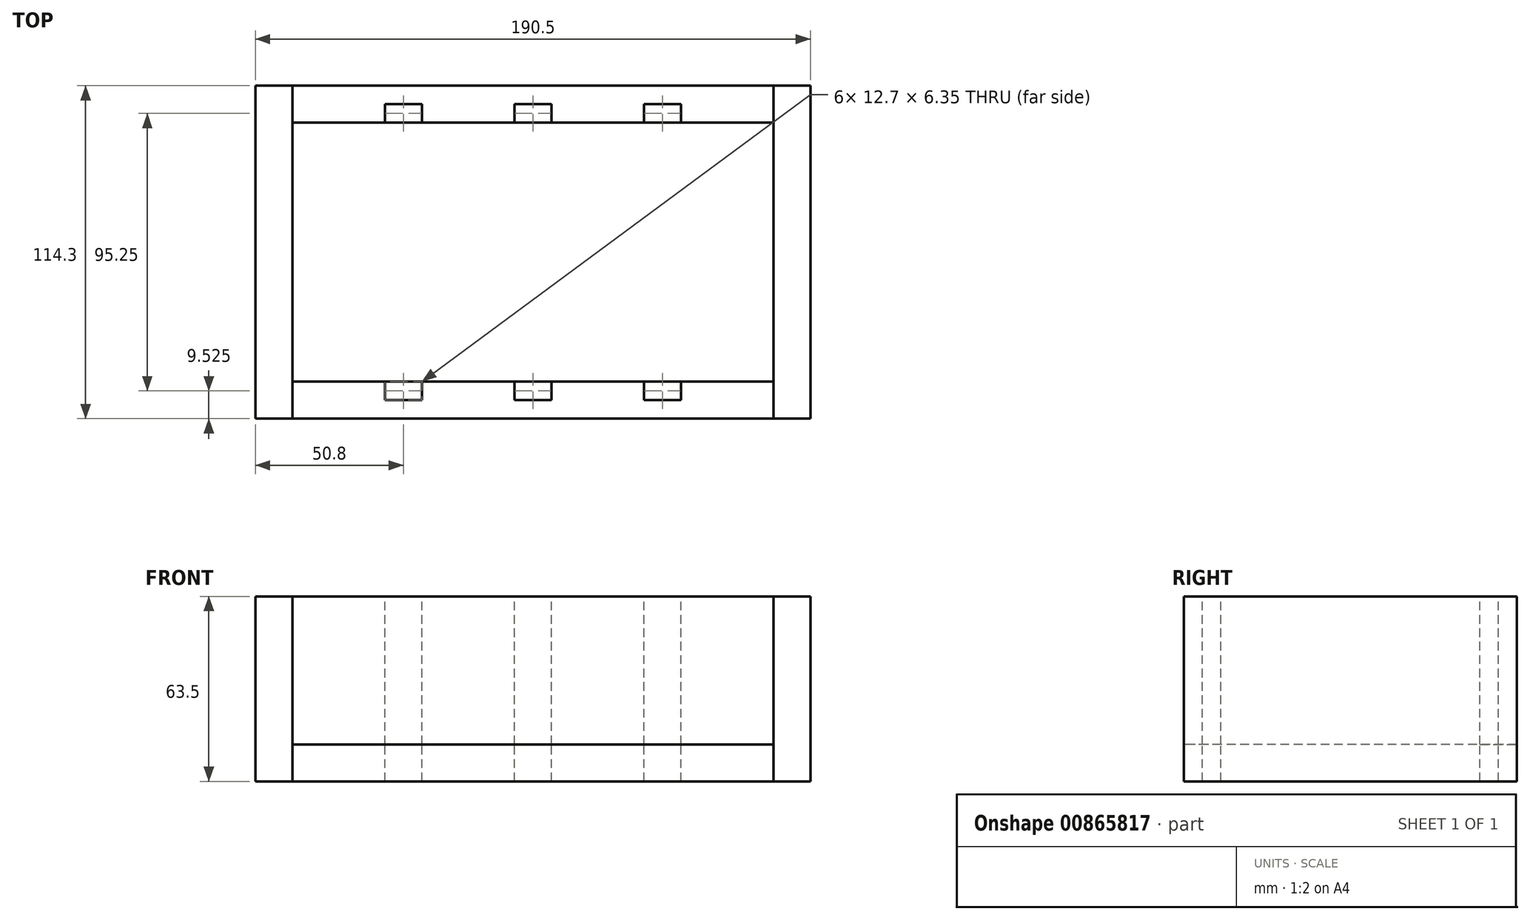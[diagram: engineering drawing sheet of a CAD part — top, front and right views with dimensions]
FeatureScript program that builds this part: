
annotation { "Feature Type Name" : "Feature", "Feature Type Description" : "" }
export const myFeature = defineFeature(function(context is Context, id is Id, definition is map)
    precondition{}
    {
        {
            var Q0;
            Q0=qCreatedBy(makeId("Top.planeOp"),FACE);
            var sketch = newSketch(context, id + "F0", { "sketchPlane" : qUnion([Q0])});
            skLineSegment(sketch, "E0.bottom", {"start": v(-82.55, 57.15) * mm, "end": v(82.55, 57.15) * mm});
            skLineSegment(sketch, "E0.top", {"start": v(-82.55, -57.15) * mm, "end": v(82.55, -57.15) * mm});
            skLineSegment(sketch, "E0.left", {"start": v(-82.55, 57.15) * mm, "end": v(-82.55, -57.15) * mm});
            skLineSegment(sketch, "E0.right", {"start": v(82.55, 57.15) * mm, "end": v(82.55, -57.15) * mm});
            skPoint(sketch, "E0.middle", {"position": v(0, 0) * mm});
            skSolve(sketch);
        }
        {
            var Q0;
            Q0=qCreatedBy(makeId("Front.planeOp"),FACE);
            var Q1;
            Q1=sQuery(id+"F0.wireOp",EDGE,"E0.bottom");
            cPlane(context, id + "F1", {"entities" : qUnion([Q0, Q1]), "cplaneType" : CPlaneType.LINE_ANGLE, "offset" : 25.4 * mm, "angle" : 0 * degree, "oppositeDirection" : true, "width" : 152.4 * mm, "height" : 152.4 * mm});
        }
        {
            var Q0;
            Q0=qCreatedBy(id+"F1.planeOp",FACE);
            var sketch = newSketch(context, id + "F2", { "sketchPlane" : qUnion([Q0])});
            skLineSegment(sketch, "E1.0.1", {"start": v(82.55, 0) * mm, "end": v(-82.55, 0) * mm});
            skLineSegment(sketch, "E1.0.3", {"start": v(-82.55, 0) * mm, "end": v(82.55, 0) * mm});
            skLineSegment(sketch, "E2.top", {"start": v(82.55, 50.8) * mm, "end": v(-82.55, 50.8) * mm});
            skLineSegment(sketch, "E2.left", {"start": v(82.55, 0) * mm, "end": v(82.55, 50.8) * mm});
            skLineSegment(sketch, "E2.right", {"start": v(-82.55, 0) * mm, "end": v(-82.55, 50.8) * mm});
            skSolve(sketch);
        }
        {
            var Q0;
            Q0=makeQuery(id+"F2.imprint","IMPRINT",FACE,{"disambiguationData":[TD([[makeQuery(id+"F2.imprint","IMPRINT",EDGE,{"derivedFrom":sQuery(id+"F2.wireOp",EDGE,"E1.0.1")}),-1.0]])]});
            extrude(context, id + "F3", {"entities" : qUnion([Q0]), "oppositeDirection" : true, "depth" : 12.7 * mm, "offsetDistance" : 25.4 * mm});
        }
        {
            var Q0;
            Q0=makeQuery(id+"F0.imprint","IMPRINT",FACE,{"disambiguationData":[TD([[makeQuery(id+"F0.imprint","IMPRINT",EDGE,{"derivedFrom":sQuery(id+"F0.wireOp",EDGE,"E0.bottom")}),-1.0]])]});
            extrude(context, id + "F4", {"entities" : qUnion([Q0]), "oppositeDirection" : true, "depth" : 12.7 * mm, "offsetDistance" : 25.4 * mm});
        }
        {
            var Q0;
            Q0=makeQuery(id+"F3.opExtrude","CAP_FACE",FACE,{"disambiguationData":[OSD([sQuery(id+"F2.wireOp",EDGE,"E1.0.1"),sQuery(id+"F2.wireOp",EDGE,"E2.top"),sQuery(id+"F2.wireOp",EDGE,"E2.left"),sQuery(id+"F2.wireOp",EDGE,"E2.right")])],"isStart":false});
            var Q1;
            Q1=makeQuery(id+"F4.opExtrude","CAP_EDGE",EDGE,{"disambiguationData":[OSD([sQuery(id+"F0.wireOp",EDGE,"E0.top")])],"isStart":true});
            cPlane(context, id + "F5", {"entities" : qUnion([Q0, Q1]), "cplaneType" : CPlaneType.LINE_ANGLE, "offset" : 25.4 * mm, "angle" : 0 * degree, "width" : 152.4 * mm, "height" : 152.4 * mm});
        }
        {
            var Q0;
            Q0=qCreatedBy(id+"F5.planeOp",FACE);
            var sketch = newSketch(context, id + "F6", { "sketchPlane" : qUnion([Q0])});
            skLineSegment(sketch, "E3.0.1", {"start": v(82.55, 0) * mm, "end": v(-82.55, 0) * mm});
            skLineSegment(sketch, "E3.0.3", {"start": v(-82.55, 0) * mm, "end": v(82.55, 0) * mm});
            skLineSegment(sketch, "E4.top", {"start": v(82.55, 50.8) * mm, "end": v(-82.55, 50.8) * mm});
            skLineSegment(sketch, "E4.left", {"start": v(82.55, 0) * mm, "end": v(82.55, 50.8) * mm});
            skLineSegment(sketch, "E4.right", {"start": v(-82.55, 0) * mm, "end": v(-82.55, 50.8) * mm});
            skSolve(sketch);
        }
        {
            var Q0;
            Q0=makeQuery(id+"F6.imprint","IMPRINT",FACE,{"disambiguationData":[TD([[makeQuery(id+"F6.imprint","IMPRINT",EDGE,{"derivedFrom":sQuery(id+"F6.wireOp",EDGE,"E3.0.1")}),-1.0]])]});
            extrude(context, id + "F7", {"entities" : qUnion([Q0]), "depth" : 12.7 * mm, "offsetDistance" : 25.4 * mm});
        }
        {
            var Q0;
            Q0=qCreatedBy(makeId("Right.planeOp"),FACE);
            var Q1;
            Q1=makeQuery(id+"F4.opExtrude","CAP_EDGE",EDGE,{"disambiguationData":[OSD([sQuery(id+"F0.wireOp",EDGE,"E0.right")])],"isStart":true});
            cPlane(context, id + "F8", {"entities" : qUnion([Q0, Q1]), "cplaneType" : CPlaneType.LINE_ANGLE, "offset" : 169.93 * mm, "angle" : 0 * degree, "width" : 152.4 * mm, "height" : 152.4 * mm});
        }
        {
            var Q0;
            Q0=qCreatedBy(id+"F8.planeOp",FACE);
            var sketch = newSketch(context, id + "F9", { "sketchPlane" : qUnion([Q0])});
            skLineSegment(sketch, "E5.0.0", {"start": v(57.15, 50.8) * mm, "end": v(57.15, 0) * mm});
            skLineSegment(sketch, "E5.0.1", {"start": v(57.15, 0) * mm, "end": v(44.45, 0) * mm});
            skLineSegment(sketch, "E5.0.2", {"start": v(44.45, 0) * mm, "end": v(44.45, 50.8) * mm});
            skLineSegment(sketch, "E5.0.3", {"start": v(44.45, 50.8) * mm, "end": v(57.15, 50.8) * mm});
            skLineSegment(sketch, "E6.0.0", {"start": v(-57.15, 0) * mm, "end": v(-57.15, 50.8) * mm});
            skLineSegment(sketch, "E6.0.1", {"start": v(-57.15, 50.8) * mm, "end": v(-44.45, 50.8) * mm});
            skLineSegment(sketch, "E6.0.2", {"start": v(-44.45, 50.8) * mm, "end": v(-44.45, 0) * mm});
            skLineSegment(sketch, "E6.0.3", {"start": v(-44.45, 0) * mm, "end": v(-57.15, 0) * mm});
            skLineSegment(sketch, "E7.0.0", {"start": v(-57.15, 0) * mm, "end": v(57.15, 0) * mm});
            skLineSegment(sketch, "E7.0.1", {"start": v(57.15, 0) * mm, "end": v(57.15, -12.7) * mm});
            skLineSegment(sketch, "E7.0.2", {"start": v(57.15, -12.7) * mm, "end": v(-57.15, -12.7) * mm});
            skLineSegment(sketch, "E7.0.3", {"start": v(-57.15, -12.7) * mm, "end": v(-57.15, 0) * mm});
            skLineSegment(sketch, "E8.bottom", {"start": v(57.15, 50.8) * mm, "end": v(-57.15, 50.8) * mm});
            skLineSegment(sketch, "E8.left", {"start": v(57.15, 50.8) * mm, "end": v(57.15, -12.7) * mm});
            skLineSegment(sketch, "E8.right", {"start": v(-57.15, 50.8) * mm, "end": v(-57.15, -12.7) * mm});
            skSolve(sketch);
        }
        {
            var Q0;
            {var subQ0=sQuery(id+"F9.wireOp",EDGE,"E5.0.2");Q0=makeQuery(id+"F9.imprint","IMPRINT",FACE,{"disambiguationData":[TD([[makeQuery(id+"F9.imprint","IMPRINT",EDGE,{"derivedFrom":subQ0}),1.0]])]});}
            var Q1;
            {var subQ0=sQuery(id+"F9.wireOp",EDGE,"E5.0.2");Q1=makeQuery(id+"F9.imprint","IMPRINT",FACE,{"disambiguationData":[TD([[makeQuery(id+"F9.imprint","IMPRINT",EDGE,{"derivedFrom":subQ0}),-1.0]])]});}
            var Q2;
            {var subQ0=sQuery(id+"F9.wireOp",EDGE,"E6.0.2");Q2=makeQuery(id+"F9.imprint","IMPRINT",FACE,{"disambiguationData":[TD([[makeQuery(id+"F9.imprint","IMPRINT",EDGE,{"derivedFrom":subQ0}),-1.0]])]});}
            var Q3;
            {var subQ4=sQuery(id+"F9.wireOp",EDGE,"E7.0.2");Q3=makeQuery(id+"F9.imprint","IMPRINT",FACE,{"disambiguationData":[TD([[makeQuery(id+"F9.imprint","IMPRINT",EDGE,{"derivedFrom":subQ4}),-1.0]])]});}
            extrude(context, id + "F10", {"entities" : qUnion([Q0, Q1, Q2, Q3]), "oppositeDirection" : true, "depth" : 12.7 * mm, "offsetDistance" : 25.4 * mm});
        }
        {
            var Q0;
            Q0=qCreatedBy(makeId("Right.planeOp"),FACE);
            var Q1;
            Q1=makeQuery(id+"F4.opExtrude","CAP_EDGE",EDGE,{"disambiguationData":[OSD([sQuery(id+"F0.wireOp",EDGE,"E0.left")])],"isStart":true});
            cPlane(context, id + "F11", {"entities" : qUnion([Q0, Q1]), "cplaneType" : CPlaneType.LINE_ANGLE, "offset" : 25.4 * mm, "angle" : 0 * degree, "oppositeDirection" : true, "width" : 152.4 * mm, "height" : 152.4 * mm});
        }
        {
            var Q0;
            Q0=qCreatedBy(id+"F11.planeOp",FACE);
            var sketch = newSketch(context, id + "F12", { "sketchPlane" : qUnion([Q0])});
            skLineSegment(sketch, "E9.0.0", {"start": v(-57.15, 50.8) * mm, "end": v(-57.15, 0) * mm});
            skLineSegment(sketch, "E9.0.1", {"start": v(-57.15, 0) * mm, "end": v(-44.45, 0) * mm});
            skLineSegment(sketch, "E9.0.2", {"start": v(-44.45, 0) * mm, "end": v(-44.45, 50.8) * mm});
            skLineSegment(sketch, "E9.0.3", {"start": v(-44.45, 50.8) * mm, "end": v(-57.15, 50.8) * mm});
            skLineSegment(sketch, "E10.0.0", {"start": v(57.15, 0) * mm, "end": v(57.15, 50.8) * mm});
            skLineSegment(sketch, "E10.0.1", {"start": v(57.15, 50.8) * mm, "end": v(44.45, 50.8) * mm});
            skLineSegment(sketch, "E10.0.2", {"start": v(44.45, 50.8) * mm, "end": v(44.45, 0) * mm});
            skLineSegment(sketch, "E10.0.3", {"start": v(44.45, 0) * mm, "end": v(57.15, 0) * mm});
            skLineSegment(sketch, "E11.0.0", {"start": v(57.15, 0) * mm, "end": v(-57.15, 0) * mm});
            skLineSegment(sketch, "E11.0.1", {"start": v(-57.15, 0) * mm, "end": v(-57.15, -12.7) * mm});
            skLineSegment(sketch, "E11.0.2", {"start": v(-57.15, -12.7) * mm, "end": v(57.15, -12.7) * mm});
            skLineSegment(sketch, "E11.0.3", {"start": v(57.15, -12.7) * mm, "end": v(57.15, 0) * mm});
            skLineSegment(sketch, "E12.bottom", {"start": v(-57.15, 50.8) * mm, "end": v(57.15, 50.8) * mm});
            skLineSegment(sketch, "E12.left", {"start": v(-57.15, 50.8) * mm, "end": v(-57.15, -12.7) * mm});
            skLineSegment(sketch, "E12.right", {"start": v(57.15, 50.8) * mm, "end": v(57.15, -12.7) * mm});
            skSolve(sketch);
        }
        {
            var Q0;
            {var subQ0=sQuery(id+"F12.wireOp",EDGE,"E9.0.2");Q0=makeQuery(id+"F12.imprint","IMPRINT",FACE,{"disambiguationData":[TD([[makeQuery(id+"F12.imprint","IMPRINT",EDGE,{"derivedFrom":subQ0}),-1.0]])]});}
            var Q1;
            {var subQ0=sQuery(id+"F12.wireOp",EDGE,"E10.0.2");Q1=makeQuery(id+"F12.imprint","IMPRINT",FACE,{"disambiguationData":[TD([[makeQuery(id+"F12.imprint","IMPRINT",EDGE,{"derivedFrom":subQ0}),1.0]])]});}
            var Q2;
            {var subQ4=sQuery(id+"F12.wireOp",EDGE,"E11.0.2");Q2=makeQuery(id+"F12.imprint","IMPRINT",FACE,{"disambiguationData":[TD([[makeQuery(id+"F12.imprint","IMPRINT",EDGE,{"derivedFrom":subQ4}),1.0]])]});}
            var Q3;
            {var subQ0=sQuery(id+"F12.wireOp",EDGE,"E9.0.2");Q3=makeQuery(id+"F12.imprint","IMPRINT",FACE,{"disambiguationData":[TD([[makeQuery(id+"F12.imprint","IMPRINT",EDGE,{"derivedFrom":subQ0}),1.0]])]});}
            extrude(context, id + "F13", {"entities" : qUnion([Q0, Q1, Q2, Q3]), "depth" : 12.7 * mm, "offsetDistance" : 25.4 * mm});
        }
        {
            var Q0;
            Q0=makeQuery(id+"F3.opExtrude","SWEPT_FACE",FACE,{"disambiguationData":[OSD([sQuery(id+"F2.wireOp",EDGE,"E2.top")])]});
            var sketch = newSketch(context, id + "F14", { "sketchPlane" : qUnion([Q0])});
            skLineSegment(sketch, "E13.bottom", {"start": v(-50.8, 44.45) * mm, "end": v(-38.1, 44.45) * mm});
            skLineSegment(sketch, "E13.top", {"start": v(-50.8, 50.8) * mm, "end": v(-38.1, 50.8) * mm});
            skLineSegment(sketch, "E13.left", {"start": v(-50.8, 44.45) * mm, "end": v(-50.8, 50.8) * mm});
            skLineSegment(sketch, "E13.right", {"start": v(-38.1, 44.45) * mm, "end": v(-38.1, 50.8) * mm});
            skLineSegment(sketch, "E14.bottom", {"start": v(-6.35, 44.45) * mm, "end": v(6.35, 44.45) * mm});
            skLineSegment(sketch, "E14.top", {"start": v(-6.35, 50.8) * mm, "end": v(6.35, 50.8) * mm});
            skLineSegment(sketch, "E14.left", {"start": v(-6.35, 44.45) * mm, "end": v(-6.35, 50.8) * mm});
            skLineSegment(sketch, "E14.right", {"start": v(6.35, 44.45) * mm, "end": v(6.35, 50.8) * mm});
            skLineSegment(sketch, "E15.bottom", {"start": v(38.1, 44.45) * mm, "end": v(50.8, 44.45) * mm});
            skLineSegment(sketch, "E15.top", {"start": v(38.1, 50.8) * mm, "end": v(50.8, 50.8) * mm});
            skLineSegment(sketch, "E15.left", {"start": v(38.1, 44.45) * mm, "end": v(38.1, 50.8) * mm});
            skLineSegment(sketch, "E15.right", {"start": v(50.8, 44.45) * mm, "end": v(50.8, 50.8) * mm});
            skLineSegment(sketch, "E16.0.0", {"start": v(82.55, 57.15) * mm, "end": v(-82.55, 57.15) * mm});
            skLineSegment(sketch, "E16.0.1", {"start": v(-82.55, 57.15) * mm, "end": v(-82.55, 44.45) * mm});
            skLineSegment(sketch, "E16.0.2", {"start": v(-82.55, 44.45) * mm, "end": v(82.55, 44.45) * mm});
            skLineSegment(sketch, "E16.0.3", {"start": v(82.55, 44.45) * mm, "end": v(82.55, 57.15) * mm});
            skLineSegment(sketch, "E17", {"start": v(0, 57.15) * mm, "end": v(0, 72.28) * mm, "construction": true});
            skLineSegment(sketch, "E18", {"start": v(0, 57.15) * mm, "end": v(0, 50.8) * mm, "construction": true});
            skLineSegment(sketch, "E19", {"start": v(-44.45, 57.15) * mm, "end": v(-44.45, 44.45) * mm, "construction": true});
            skLineSegment(sketch, "E20", {"start": v(44.45, 57.15) * mm, "end": v(44.45, 44.45) * mm, "construction": true});
            skPoint(sketch, "E21", {"position": v(-44.45, 50.8) * mm});
            skPoint(sketch, "E22", {"position": v(44.45, 50.8) * mm});
            skSolve(sketch);
        }
        {
            var Q0;
            Q0=makeQuery(id+"F14.imprint","IMPRINT",FACE,{"disambiguationData":[TD([[makeQuery(id+"F14.imprint","IMPRINT",EDGE,{"derivedFrom":sQuery(id+"F14.wireOp",EDGE,"E13.top")}),-1.0]])]});
            var Q1;
            Q1=makeQuery(id+"F14.imprint","IMPRINT",FACE,{"disambiguationData":[TD([[makeQuery(id+"F14.imprint","IMPRINT",EDGE,{"derivedFrom":sQuery(id+"F14.wireOp",EDGE,"E14.top")}),-1.0]])]});
            var Q2;
            Q2=makeQuery(id+"F14.imprint","IMPRINT",FACE,{"disambiguationData":[TD([[makeQuery(id+"F14.imprint","IMPRINT",EDGE,{"derivedFrom":sQuery(id+"F14.wireOp",EDGE,"E15.top")}),-1.0]])]});
            extrude(context, id + "F15", {"entities" : qUnion([Q0, Q1, Q2]), "operationType" : NewBodyOperationType.REMOVE, "oppositeDirection" : true, "depth" : 63.5 * mm, "offsetDistance" : 25.4 * mm});
        }
        {
            var Q0;
            Q0=makeQuery(id+"F7.opExtrude","SWEPT_FACE",FACE,{"disambiguationData":[OSD([sQuery(id+"F6.wireOp",EDGE,"E4.top")])]});
            var sketch = newSketch(context, id + "F16", { "sketchPlane" : qUnion([Q0])});
            skLineSegment(sketch, "E23.bottom", {"start": v(-50.8, -44.45) * mm, "end": v(-38.1, -44.45) * mm});
            skLineSegment(sketch, "E23.top", {"start": v(-50.8, -50.8) * mm, "end": v(-38.1, -50.8) * mm});
            skLineSegment(sketch, "E23.left", {"start": v(-50.8, -44.45) * mm, "end": v(-50.8, -50.8) * mm});
            skLineSegment(sketch, "E23.right", {"start": v(-38.1, -44.45) * mm, "end": v(-38.1, -50.8) * mm});
            skLineSegment(sketch, "E24.bottom", {"start": v(-6.35, -44.45) * mm, "end": v(6.35, -44.45) * mm});
            skLineSegment(sketch, "E24.top", {"start": v(-6.35, -50.8) * mm, "end": v(6.35, -50.8) * mm});
            skLineSegment(sketch, "E24.left", {"start": v(-6.35, -44.45) * mm, "end": v(-6.35, -50.8) * mm});
            skLineSegment(sketch, "E24.right", {"start": v(6.35, -44.45) * mm, "end": v(6.35, -50.8) * mm});
            skLineSegment(sketch, "E25.bottom", {"start": v(38.1, -44.45) * mm, "end": v(50.8, -44.45) * mm});
            skLineSegment(sketch, "E25.top", {"start": v(38.1, -50.8) * mm, "end": v(50.8, -50.8) * mm});
            skLineSegment(sketch, "E25.left", {"start": v(38.1, -44.45) * mm, "end": v(38.1, -50.8) * mm});
            skLineSegment(sketch, "E25.right", {"start": v(50.8, -44.45) * mm, "end": v(50.8, -50.8) * mm});
            skLineSegment(sketch, "E26", {"start": v(0, -57.15) * mm, "end": v(0, -59) * mm, "construction": true});
            skPoint(sketch, "E26.endSnap0", {"position": v(0, -57.15) * mm});
            skLineSegment(sketch, "E27.0.0", {"start": v(-82.55, -57.15) * mm, "end": v(82.55, -57.15) * mm});
            skLineSegment(sketch, "E27.0.1", {"start": v(82.55, -57.15) * mm, "end": v(82.55, -44.45) * mm});
            skLineSegment(sketch, "E27.0.2", {"start": v(82.55, -44.45) * mm, "end": v(-82.55, -44.45) * mm});
            skLineSegment(sketch, "E27.0.3", {"start": v(-82.55, -44.45) * mm, "end": v(-82.55, -57.15) * mm});
            skLineSegment(sketch, "E28", {"start": v(0, -50.8) * mm, "end": v(0, -57.15) * mm, "construction": true});
            skLineSegment(sketch, "E29", {"start": v(44.45, -44.45) * mm, "end": v(44.45, -57.15) * mm, "construction": true});
            skLineSegment(sketch, "E30", {"start": v(-44.45, -44.45) * mm, "end": v(-44.45, -57.15) * mm, "construction": true});
            skPoint(sketch, "E31", {"position": v(-44.45, -50.8) * mm});
            skPoint(sketch, "E32", {"position": v(44.45, -50.8) * mm});
            skSolve(sketch);
        }
        {
            var Q0;
            Q0=makeQuery(id+"F16.imprint","IMPRINT",FACE,{"disambiguationData":[TD([[makeQuery(id+"F16.imprint","IMPRINT",EDGE,{"derivedFrom":sQuery(id+"F16.wireOp",EDGE,"E25.top")}),1.0]])]});
            var Q1;
            Q1=makeQuery(id+"F16.imprint","IMPRINT",FACE,{"disambiguationData":[TD([[makeQuery(id+"F16.imprint","IMPRINT",EDGE,{"derivedFrom":sQuery(id+"F16.wireOp",EDGE,"E24.top")}),1.0]])]});
            var Q2;
            Q2=makeQuery(id+"F16.imprint","IMPRINT",FACE,{"disambiguationData":[TD([[makeQuery(id+"F16.imprint","IMPRINT",EDGE,{"derivedFrom":sQuery(id+"F16.wireOp",EDGE,"E23.top")}),1.0]])]});
            extrude(context, id + "F17", {"entities" : qUnion([Q0, Q1, Q2]), "operationType" : NewBodyOperationType.REMOVE, "oppositeDirection" : true, "depth" : 63.5 * mm, "offsetDistance" : 25.4 * mm});
        }
    });
